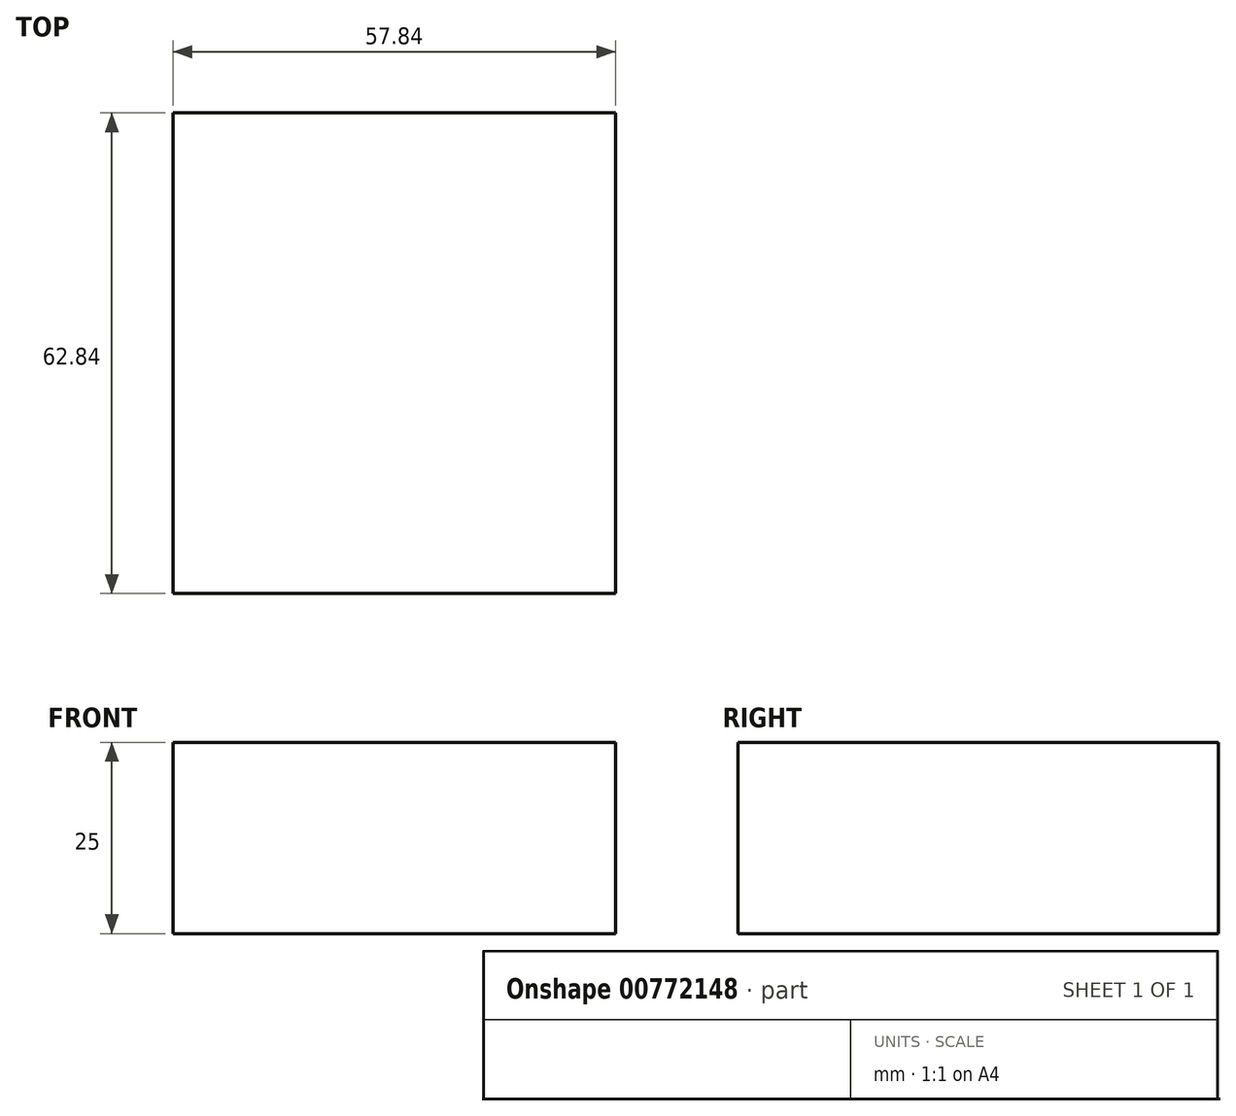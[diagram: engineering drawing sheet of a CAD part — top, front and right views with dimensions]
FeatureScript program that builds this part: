
annotation { "Feature Type Name" : "Feature", "Feature Type Description" : "" }
export const myFeature = defineFeature(function(context is Context, id is Id, definition is map)
    precondition{}
    {
        {
            var Q0;
            Q0=qCreatedBy(makeId("Top.planeOp"),FACE);
            var sketch = newSketch(context, id + "F0", { "sketchPlane" : qUnion([Q0])});
            skLineSegment(sketch, "E0.bottom", {"start": v(28.92, -31.42) * mm, "end": v(-28.92, -31.42) * mm});
            skLineSegment(sketch, "E0.top", {"start": v(28.92, 31.42) * mm, "end": v(-28.92, 31.42) * mm});
            skLineSegment(sketch, "E0.left", {"start": v(28.92, -31.42) * mm, "end": v(28.92, 31.42) * mm});
            skLineSegment(sketch, "E0.right", {"start": v(-28.92, -31.42) * mm, "end": v(-28.92, 31.42) * mm});
            skPoint(sketch, "E0.middle", {"position": v(0, 0) * mm});
            skSolve(sketch);
        }
        {
            var Q0;
            Q0 = qSketchRegion(id + "F0", true);
            extrude(context, id + "F1", {"entities" : qUnion([Q0]), "depth" : 25 * mm, "offsetDistance" : 25 * mm});
        }
    });
